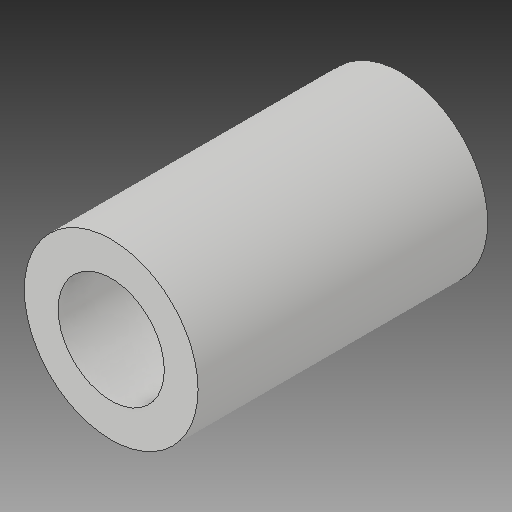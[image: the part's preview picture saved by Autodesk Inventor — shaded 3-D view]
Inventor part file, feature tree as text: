
AUTODESK INVENTOR PART (.ipt)
format: ipt  version: 2018 (Build 220112000, 112)  size: 105,984 bytes
history: native  units: mm
features: other x3, sketch x1
ambient origin geometry x8: Origin, YZ Plane, XZ Plane, XY Plane, X Axis, Y Axis, Z Axis, Center Point
bodies: Solid1 (feature_tree)
feature tree (4):
  other  "Long-Spacer.ipt"
  other  "Solid1::Long-Spacer.ipt"
  other  "TaggingFeature1"
  sketch  "Sketch1"  dims[d0=10.0mm]
